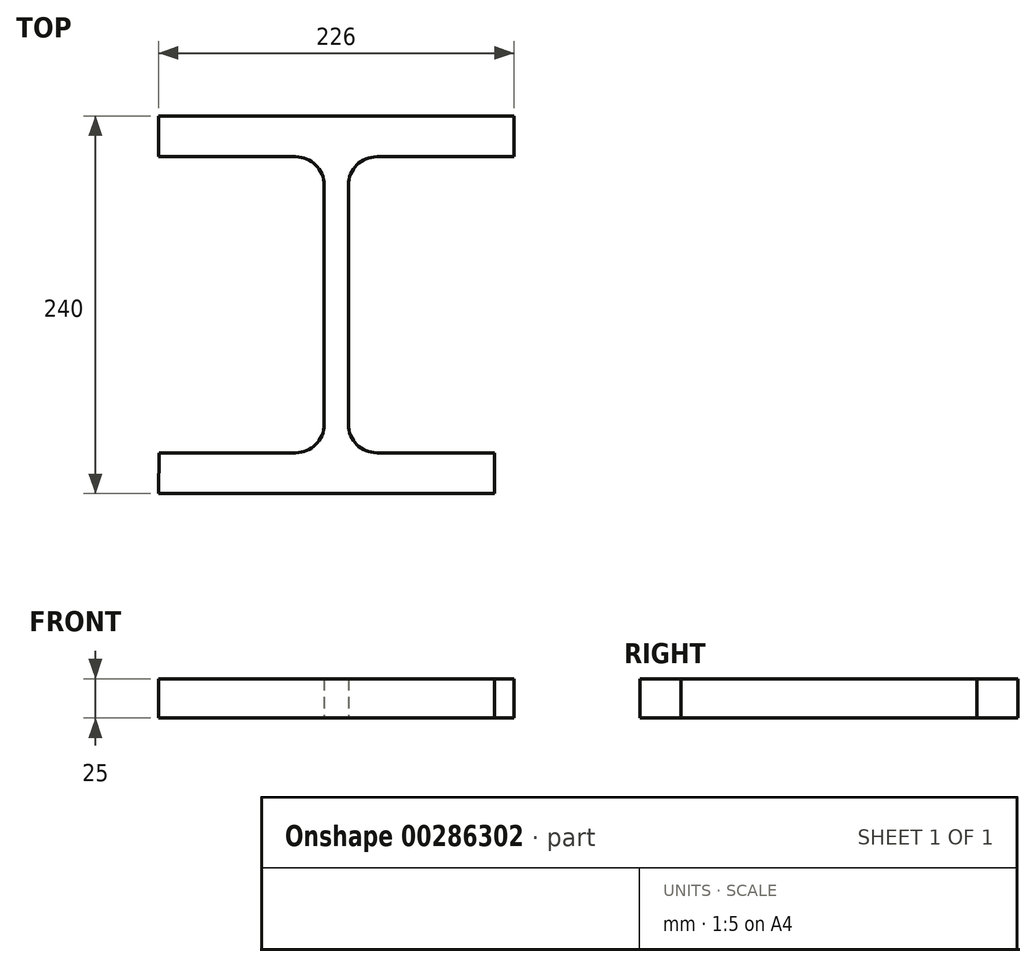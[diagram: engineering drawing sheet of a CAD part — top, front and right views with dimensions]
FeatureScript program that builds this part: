
annotation { "Feature Type Name" : "Feature", "Feature Type Description" : "" }
export const myFeature = defineFeature(function(context is Context, id is Id, definition is map)
    precondition{}
    {
        {
            var Q0;
            Q0=qCreatedBy(makeId("Top.planeOp"),FACE);
            var sketch = newSketch(context, id + "F0", { "sketchPlane" : qUnion([Q0])});
            skLineSegment(sketch, "E0", {"start": v(-104.44, 52.76) * mm, "end": v(121.56, 52.76) * mm});
            skLineSegment(sketch, "E1", {"start": v(-104.44, 52.76) * mm, "end": v(-104.44, 26.76) * mm});
            skLineSegment(sketch, "E2", {"start": v(-104.44, 26.76) * mm, "end": v(-17.19, 26.76) * mm});
            skLineSegment(sketch, "E3", {"start": v(121.56, 52.76) * mm, "end": v(121.56, 26.76) * mm});
            skLineSegment(sketch, "E4", {"start": v(-103.9, -161.25) * mm, "end": v(-17.19, -161.25) * mm});
            skLineSegment(sketch, "E5", {"start": v(109.1, -161.25) * mm, "end": v(109.1, -187.24) * mm});
            skLineSegment(sketch, "E6", {"start": v(109.1, -187.24) * mm, "end": v(-104.44, -187.24) * mm});
            skLineSegment(sketch, "E7", {"start": v(-104.44, -187.24) * mm, "end": v(-103.9, -161.25) * mm});
            skLineSegment(sketch, "E8", {"start": v(121.56, 26.76) * mm, "end": v(34.31, 26.76) * mm});
            skLineSegment(sketch, "E9", {"start": v(0.81, 8.76) * mm, "end": v(0.81, -143.25) * mm});
            skLineSegment(sketch, "E10", {"start": v(16.31, 8.76) * mm, "end": v(16.31, -143.25) * mm});
            skLineSegment(sketch, "E11.trimOffspring", {"start": v(34.31, 26.76) * mm, "end": v(121.56, 26.76) * mm});
            skLineSegment(sketch, "E12.trimOffspring", {"start": v(34.31, -161.25) * mm, "end": v(109.1, -161.25) * mm});
            skPoint(sketch, "E13.visualSharp", {"position": v(0.81, 26.76) * mm});
            skArc(sketch, "E13.filletArc", {"start": v(0.81, 8.76) * mm, "mid": v(-4.46, 21.49) * mm, "end": v(-17.19, 26.76) * mm});
            skPoint(sketch, "E14.visualSharp", {"position": v(16.31, 26.76) * mm});
            skArc(sketch, "E14.filletArc", {"start": v(34.31, 26.76) * mm, "mid": v(21.58, 21.49) * mm, "end": v(16.31, 8.76) * mm});
            skPoint(sketch, "E15.visualSharp", {"position": v(16.31, -161.25) * mm});
            skArc(sketch, "E15.filletArc", {"start": v(16.31, -143.25) * mm, "mid": v(21.58, -155.98) * mm, "end": v(34.31, -161.25) * mm});
            skPoint(sketch, "E16.visualSharp", {"position": v(0.81, -161.25) * mm});
            skArc(sketch, "E16.filletArc", {"start": v(-17.19, -161.25) * mm, "mid": v(-4.46, -155.98) * mm, "end": v(0.81, -143.25) * mm});
            skSolve(sketch);
        }
        {
            var Q0;
            Q0 = qSketchRegion(id + "F0", true);
            extrude(context, id + "F1", {"entities" : qUnion([Q0]), "depth" : 25 * mm});
        }
    });
